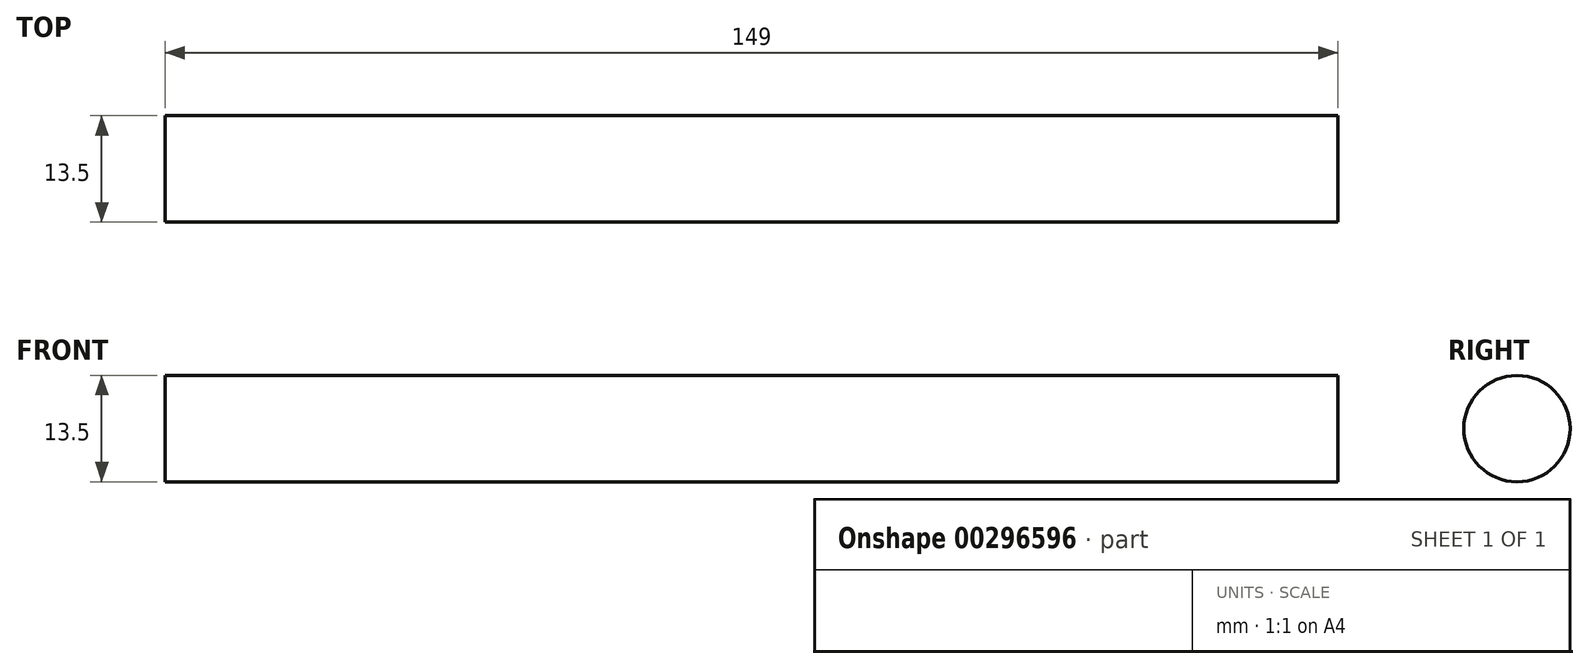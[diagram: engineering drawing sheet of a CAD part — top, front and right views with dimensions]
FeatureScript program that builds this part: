
annotation { "Feature Type Name" : "Feature", "Feature Type Description" : "" }
export const myFeature = defineFeature(function(context is Context, id is Id, definition is map)
    precondition{}
    {
        {
            var Q0;
            Q0=qCreatedBy(makeId("Right.planeOp"),FACE);
            var sketch = newSketch(context, id + "F0", { "sketchPlane" : qUnion([Q0])});
            skCircle(sketch, "E0", {"center": v(0, 0) * mm, "radius": 6.75 * mm});
            skSolve(sketch);
        }
        {
            var Q0;
            Q0 = qSketchRegion(id + "F0", true);
            extrude(context, id + "F1", {"entities" : qUnion([Q0]), "depth" : 149 * mm});
        }
    });
